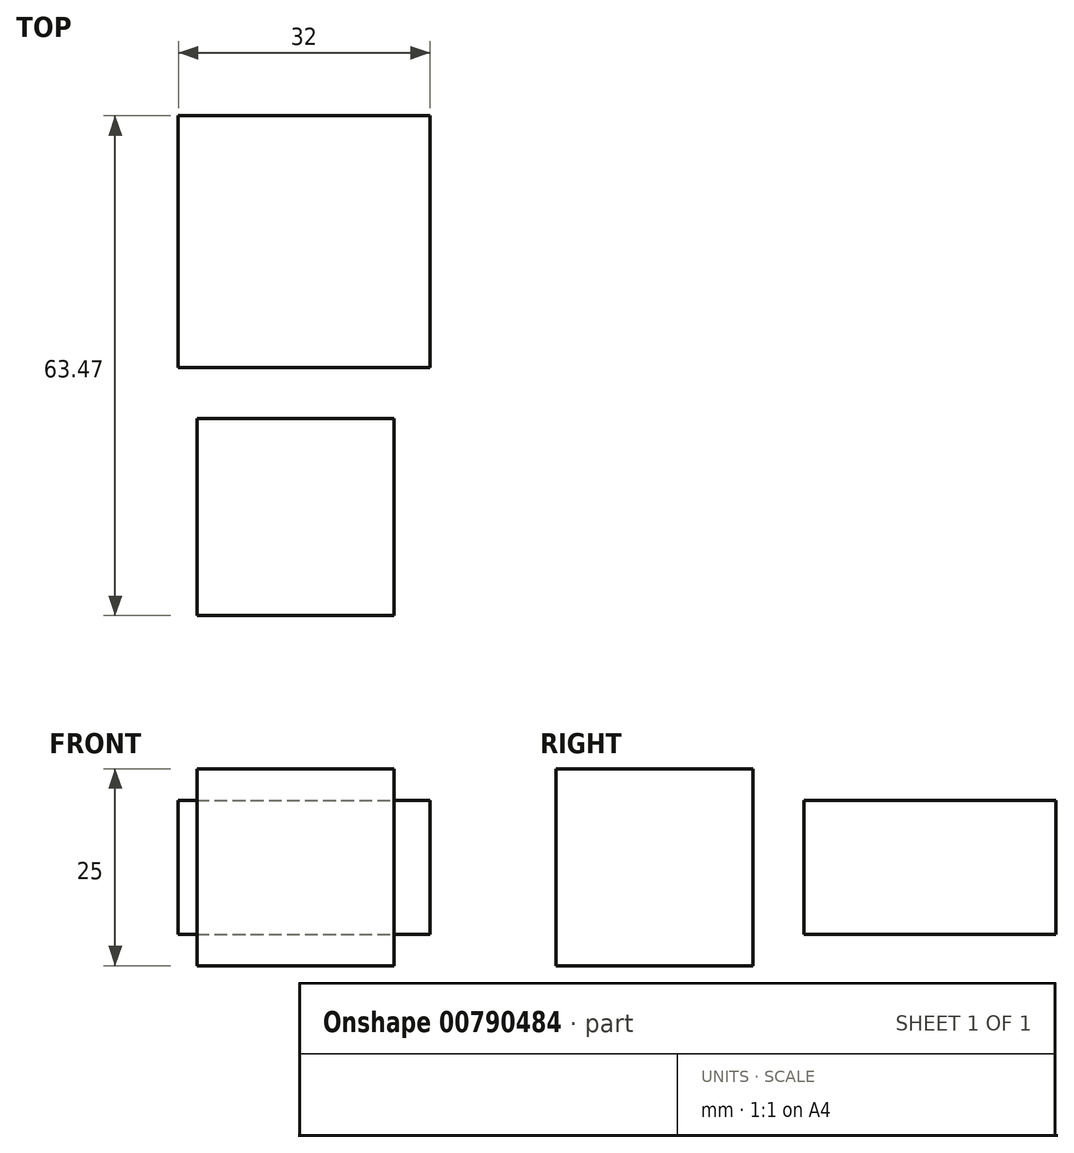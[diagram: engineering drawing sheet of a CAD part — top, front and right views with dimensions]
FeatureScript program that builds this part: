
annotation { "Feature Type Name" : "Feature", "Feature Type Description" : "" }
export const myFeature = defineFeature(function(context is Context, id is Id, definition is map)
    precondition{}
    {
        {
            var Q0;
            Q0=qCreatedBy(makeId("Top.planeOp"),FACE);
            var sketch = newSketch(context, id + "F0", { "sketchPlane" : qUnion([Q0])});
            skLineSegment(sketch, "E0.bottom", {"start": v(0, 0) * mm, "end": v(25, 0) * mm});
            skLineSegment(sketch, "E0.top", {"start": v(0, -25) * mm, "end": v(25, -25) * mm});
            skLineSegment(sketch, "E0.left", {"start": v(0, 0) * mm, "end": v(0, -25) * mm});
            skLineSegment(sketch, "E0.right", {"start": v(25, 0) * mm, "end": v(25, -25) * mm});
            skSolve(sketch);
        }
        {
            var Q0;
            Q0=makeQuery(id+"F0.imprint","IMPRINT",FACE,{"disambiguationData":[TD([[makeQuery(id+"F0.imprint","IMPRINT",EDGE,{"derivedFrom":sQuery(id+"F0.wireOp",EDGE,"E0.bottom")}),-1.0]])]});
            extrude(context, id + "F1", {"entities" : qUnion([Q0]), "depth" : (25 / 2) * mm, "offsetDistance" : 25 * mm, "hasSecondDirection" : true, "secondDirectionOppositeDirection" : true, "secondDirectionDepth" : (25 / 2) * mm});
        }
        {
            var Q0;
            Q0=qCreatedBy(makeId("Top.planeOp"),FACE);
            var sketch = newSketch(context, id + "F2", { "sketchPlane" : qUnion([Q0])});
            skLineSegment(sketch, "E1.bottom", {"start": v(-2.41, 38.47) * mm, "end": v(29.59, 38.47) * mm});
            skLineSegment(sketch, "E1.top", {"start": v(-2.41, 6.47) * mm, "end": v(29.59, 6.47) * mm});
            skLineSegment(sketch, "E1.left", {"start": v(-2.41, 38.47) * mm, "end": v(-2.41, 6.47) * mm});
            skLineSegment(sketch, "E1.right", {"start": v(29.59, 38.47) * mm, "end": v(29.59, 6.47) * mm});
            skSolve(sketch);
        }
        {
            var Q0;
            Q0=makeQuery(id+"F2.imprint","IMPRINT",FACE,{"disambiguationData":[TD([[makeQuery(id+"F2.imprint","IMPRINT",EDGE,{"derivedFrom":sQuery(id+"F2.wireOp",EDGE,"E1.bottom")}),-1.0]])]});
            extrude(context, id + "F3", {"entities" : qUnion([Q0]), "depth" : (17 / 2) * mm, "offsetDistance" : 25 * mm, "hasSecondDirection" : true, "secondDirectionOppositeDirection" : true, "secondDirectionDepth" : (17 / 2) * mm});
        }
    });
